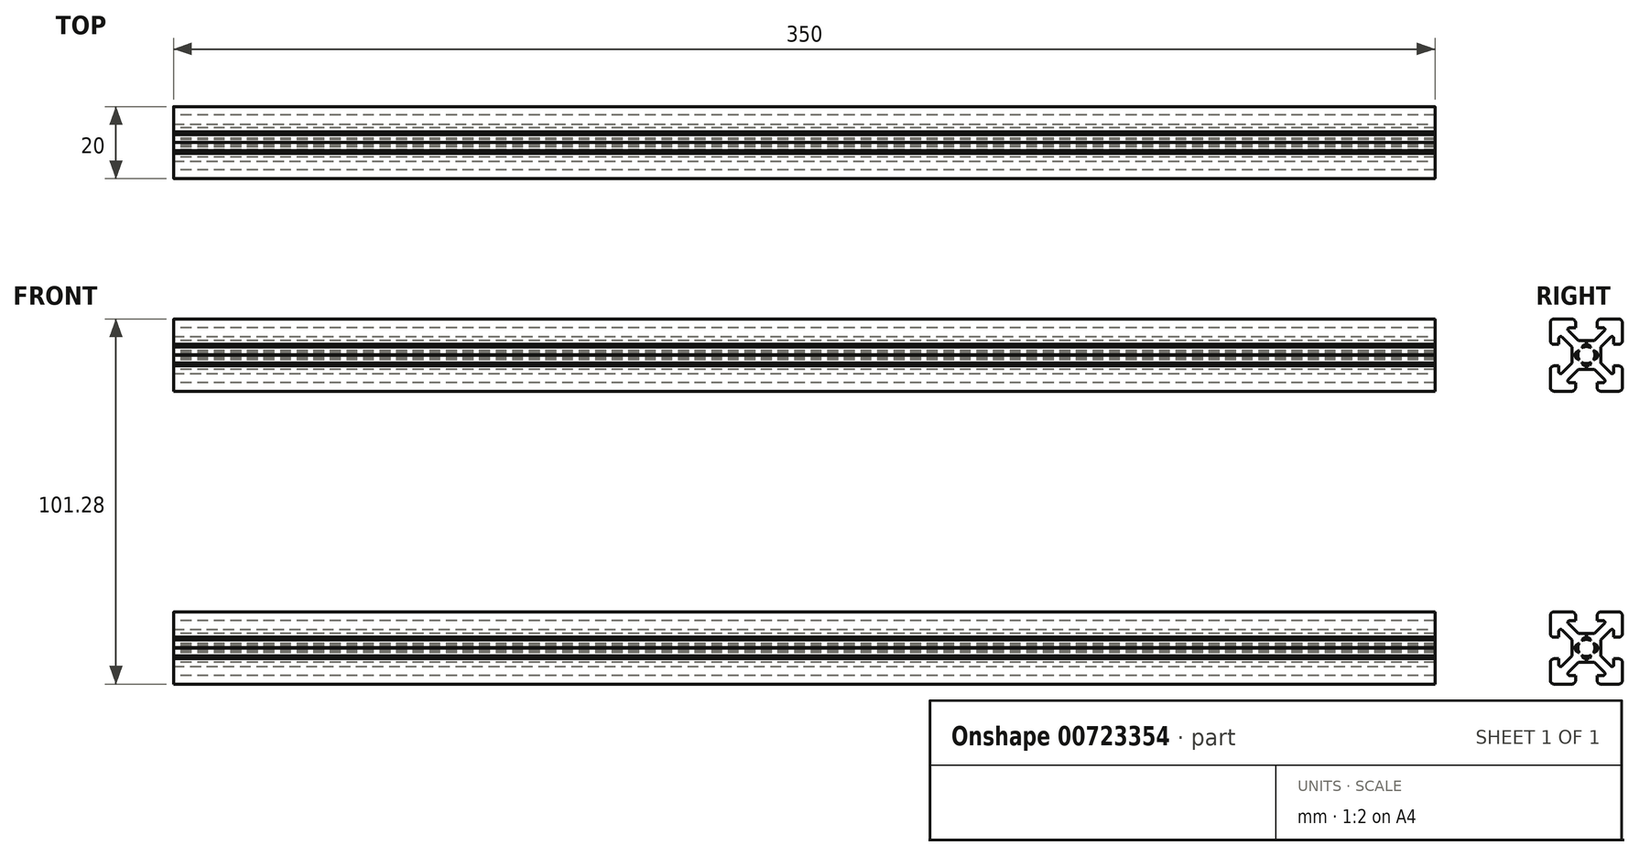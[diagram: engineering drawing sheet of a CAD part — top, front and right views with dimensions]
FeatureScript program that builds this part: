
annotation { "Feature Type Name" : "Feature", "Feature Type Description" : "" }
export const myFeature = defineFeature(function(context is Context, id is Id, definition is map)
    precondition{}
    {
        {
            var Q0;
            Q0=qCreatedBy(makeId("Top.planeOp"),FACE);
            var sketch = newSketch(context, id + "F0", { "sketchPlane" : qUnion([Q0])});
            skLineSegment(sketch, "E0", {"start": v(-15.81, 0) * mm, "end": v(2.4, 0) * mm, "construction": true});
            skLineSegment(sketch, "E1", {"start": v(0, 15.89) * mm, "end": v(0, -13.7) * mm, "construction": true});
            skLineSegment(sketch, "E2", {"start": v(0, 0) * mm, "end": v(-1.66, 1.66) * mm, "construction": true});
            skLineSegment(sketch, "E3", {"start": v(-2.3, 4.06) * mm, "end": v(-5.86, 7.63) * mm});
            skLineSegment(sketch, "E4", {"start": v(-5.86, 7.63) * mm, "end": v(-3, 7.63) * mm});
            skLineSegment(sketch, "E5", {"start": v(-3, 7.63) * mm, "end": v(-3, 10) * mm});
            skLineSegment(sketch, "E6", {"start": v(-3, 10) * mm, "end": v(-10, 10) * mm});
            skLineSegment(sketch, "E7.MirrorCS", {"start": v(-4, 2.23) * mm, "end": v(-7.63, 5.86) * mm});
            skLineSegment(sketch, "E8.MirrorCS", {"start": v(-7.63, 3) * mm, "end": v(-10, 3) * mm});
            skLineSegment(sketch, "E9.MirrorCS", {"start": v(-10, 3) * mm, "end": v(-10, 10) * mm});
            skLineSegment(sketch, "E10.MirrorCS", {"start": v(-7.63, 5.86) * mm, "end": v(-7.63, 3) * mm});
            skLineSegment(sketch, "E11.MirrorCS", {"start": v(3, 10) * mm, "end": v(10, 10) * mm});
            skLineSegment(sketch, "E12.MirrorCS", {"start": v(5.86, 7.63) * mm, "end": v(3, 7.63) * mm});
            skLineSegment(sketch, "E13.MirrorCS", {"start": v(3, 7.63) * mm, "end": v(3, 10) * mm});
            skLineSegment(sketch, "E14.MirrorCS", {"start": v(7.63, 5.86) * mm, "end": v(7.63, 3) * mm});
            skLineSegment(sketch, "E15.MirrorCS", {"start": v(10, 3) * mm, "end": v(10, 10) * mm});
            skLineSegment(sketch, "E16.MirrorCS", {"start": v(7.63, 3) * mm, "end": v(10, 3) * mm});
            skLineSegment(sketch, "E17.MirrorCS", {"start": v(2.3, 4.06) * mm, "end": v(5.86, 7.63) * mm});
            skLineSegment(sketch, "E18.MirrorCS", {"start": v(4, 2.23) * mm, "end": v(7.63, 5.86) * mm});
            skLineSegment(sketch, "E19.MirrorCS", {"start": v(5.86, -7.63) * mm, "end": v(3, -7.63) * mm});
            skLineSegment(sketch, "E20.MirrorCS", {"start": v(3, -10) * mm, "end": v(10, -10) * mm});
            skLineSegment(sketch, "E21.MirrorCS", {"start": v(-5.86, -7.63) * mm, "end": v(-3, -7.63) * mm});
            skLineSegment(sketch, "E22.MirrorCS", {"start": v(-3, -10) * mm, "end": v(-10, -10) * mm});
            skLineSegment(sketch, "E23.MirrorCS", {"start": v(-3, -7.63) * mm, "end": v(-3, -10) * mm});
            skLineSegment(sketch, "E24.MirrorCS", {"start": v(3, -7.63) * mm, "end": v(3, -10) * mm});
            skLineSegment(sketch, "E25.MirrorCS", {"start": v(7.63, -5.86) * mm, "end": v(7.63, -3) * mm});
            skLineSegment(sketch, "E26.MirrorCS", {"start": v(10, -3) * mm, "end": v(10, -10) * mm});
            skLineSegment(sketch, "E27.MirrorCS", {"start": v(4, -2.23) * mm, "end": v(7.63, -5.86) * mm});
            skLineSegment(sketch, "E28.MirrorCS", {"start": v(-7.63, -5.86) * mm, "end": v(-7.63, -3) * mm});
            skLineSegment(sketch, "E29.MirrorCS", {"start": v(-10, -3) * mm, "end": v(-10, -10) * mm});
            skLineSegment(sketch, "E30.MirrorCS", {"start": v(-7.63, -3) * mm, "end": v(-10, -3) * mm});
            skLineSegment(sketch, "E31.MirrorCS", {"start": v(-4, -2.23) * mm, "end": v(-7.63, -5.86) * mm});
            skLineSegment(sketch, "E32.MirrorCS", {"start": v(2.23, -4) * mm, "end": v(5.86, -7.63) * mm});
            skLineSegment(sketch, "E33.MirrorCS", {"start": v(-2.23, -4) * mm, "end": v(-5.86, -7.63) * mm});
            skLineSegment(sketch, "E34.MirrorCS", {"start": v(7.63, -3) * mm, "end": v(10, -3) * mm});
            skLineSegment(sketch, "E35", {"start": v(-4, 0) * mm, "end": v(-4, 0) * mm});
            skLineSegment(sketch, "E36", {"start": v(-2.3, 4.06) * mm, "end": v(-0.02, 4.06) * mm});
            skLineSegment(sketch, "E37.MirrorCS", {"start": v(-15.81, 8.12) * mm, "end": v(21.32, 8.12) * mm, "construction": true});
            skLineSegment(sketch, "E38", {"start": v(-4, 2.23) * mm, "end": v(-4, 0.02) * mm});
            skLineSegment(sketch, "E39", {"start": v(-2.23, -4) * mm, "end": v(-0.05, -4) * mm});
            skLineSegment(sketch, "E40", {"start": v(4, 2.23) * mm, "end": v(4, 0.03) * mm});
            skPoint(sketch, "E41.orphan", {"position": v(-0.59, 2.36) * mm});
            skPoint(sketch, "E42.orphan", {"position": v(-2.36, 0.59) * mm});
            skLineSegment(sketch, "E43.trimOffspring", {"start": v(0.03, 4.06) * mm, "end": v(2.3, 4.06) * mm});
            skPoint(sketch, "E44.orphan", {"position": v(0.59, 2.36) * mm});
            skPoint(sketch, "E45.orphan", {"position": v(2.36, 0.59) * mm});
            skPoint(sketch, "E46.orphan", {"position": v(-2.36, -0.59) * mm});
            skPoint(sketch, "E47.orphan", {"position": v(-0.59, -2.36) * mm});
            skPoint(sketch, "E48.orphan", {"position": v(0.59, -2.36) * mm});
            skPoint(sketch, "E49.orphan", {"position": v(2.36, -0.59) * mm});
            skLineSegment(sketch, "E50", {"start": v(-2.4, 0.03) * mm, "end": v(-2.4, 0.03) * mm});
            skLineSegment(sketch, "E51.MirrorCS", {"start": v(-2.4, -0.03) * mm, "end": v(-2.4, -0.03) * mm});
            skLineSegment(sketch, "E52.MirrorCS", {"start": v(2.4, 0.03) * mm, "end": v(2.4, 0.03) * mm});
            skLineSegment(sketch, "E53.MirrorCS", {"start": v(2.4, -0.03) * mm, "end": v(2.4, -0.03) * mm});
            skLineSegment(sketch, "E54.trimOffspring", {"start": v(4, -0.03) * mm, "end": v(4, -2.23) * mm});
            skLineSegment(sketch, "E55.trimOffspring", {"start": v(-4, -0.03) * mm, "end": v(-4, -2.23) * mm});
            skPoint(sketch, "E56.end.orphan", {"position": v(-2.4, 0) * mm});
            skPoint(sketch, "E57.orphan", {"position": v(-4, 0.03) * mm});
            skPoint(sketch, "E58.MirrorCS.end.orphan", {"position": v(2.4, 0) * mm});
            skPoint(sketch, "E58.MirrorCS.start.orphan", {"position": v(2.4, -0.03) * mm});
            skPoint(sketch, "E59.MirrorCS.start.orphan", {"position": v(2.4, 0.03) * mm});
            skLineSegment(sketch, "E60.trimOffspring", {"start": v(0.05, -4) * mm, "end": v(2.23, -4) * mm});
            skLineSegment(sketch, "E61", {"start": v(0, 0) * mm, "end": v(10, 10) * mm, "construction": true});
            skLineSegment(sketch, "E62", {"start": v(0, 0) * mm, "end": v(-10, -10) * mm, "construction": true});
            skLineSegment(sketch, "E63", {"start": v(10, -10) * mm, "end": v(0.07, 0.07) * mm, "construction": true});
            skPoint(sketch, "E64.start.orphan", {"position": v(-4, -0.03) * mm});
            skLineSegment(sketch, "E65", {"start": v(-2.82, -0.78) * mm, "end": v(-1.9, -1.37) * mm});
            skPoint(sketch, "E66.orphan", {"position": v(-1.66, -1.66) * mm});
            skPoint(sketch, "E67.orphan", {"position": v(0.03, -4.06) * mm});
            skPoint(sketch, "E68.orphan", {"position": v(-0.03, -4.06) * mm});
            skLineSegment(sketch, "E69", {"start": v(-2.82, 0.8) * mm, "end": v(-1.87, 1.41) * mm});
            skLineSegment(sketch, "E70", {"start": v(-0.76, 2.95) * mm, "end": v(-1.54, 1.77) * mm});
            skLineSegment(sketch, "E71", {"start": v(0.76, 2.95) * mm, "end": v(1.51, 1.8) * mm});
            skLineSegment(sketch, "E72", {"start": v(2.82, 0.8) * mm, "end": v(1.83, 1.46) * mm});
            skLineSegment(sketch, "E73", {"start": v(2.82, -0.8) * mm, "end": v(1.87, -1.41) * mm});
            skLineSegment(sketch, "E74.trimOffspring", {"start": v(1.8, -1.68) * mm, "end": v(1.82, -1.66) * mm});
            skLineSegment(sketch, "E75.trimOffspring", {"start": v(-8.12, 8.12) * mm, "end": v(-29.35, 29.35) * mm, "construction": true});
            skLineSegment(sketch, "E76", {"start": v(0.74, -2.96) * mm, "end": v(1.51, -1.8) * mm});
            skPoint(sketch, "E77.trimOffspring.start.orphan", {"position": v(0.33, -2.4) * mm});
            skPoint(sketch, "E78.MirrorCS.end.orphan", {"position": v(-0.33, -2.4) * mm});
            skLineSegment(sketch, "E79.trimOffspring", {"start": v(2.43, 0) * mm, "end": v(21.32, 0) * mm, "construction": true});
            skPoint(sketch, "E80.trimOffspring.start.orphan", {"position": v(0.33, 2.4) * mm});
            skPoint(sketch, "E81.trimOffspring.start.orphan", {"position": v(-0.33, 2.4) * mm});
            skArc(sketch, "E82", {"start": v(-1.87, 1.41) * mm, "mid": v(-2.35, 0.03) * mm, "end": v(-1.9, -1.37) * mm});
            skArc(sketch, "E83.trimOffspring", {"start": v(1.51, 1.8) * mm, "mid": v(-0.02, 2.35) * mm, "end": v(-1.54, 1.77) * mm});
            skArc(sketch, "E84.trimOffspring", {"start": v(1.87, -1.41) * mm, "mid": v(2.35, 0.03) * mm, "end": v(1.83, 1.46) * mm});
            skArc(sketch, "E85.trimOffspring", {"start": v(-1.55, -1.76) * mm, "mid": v(-0.03, -2.35) * mm, "end": v(1.51, -1.8) * mm});
            skLineSegment(sketch, "E86", {"start": v(-1.55, -1.76) * mm, "end": v(-0.75, -2.96) * mm});
            skLineSegment(sketch, "E87", {"start": v(-4, 0.03) * mm, "end": v(-2.82, 0.03) * mm});
            skLineSegment(sketch, "E88", {"start": v(-2.82, 0.03) * mm, "end": v(-2.82, 0.8) * mm});
            skLineSegment(sketch, "E89", {"start": v(-4, -0.03) * mm, "end": v(-2.82, -0.03) * mm});
            skLineSegment(sketch, "E90", {"start": v(-2.82, -0.03) * mm, "end": v(-2.82, -0.78) * mm});
            skLineSegment(sketch, "E91.MirrorCS", {"start": v(4, 0.03) * mm, "end": v(2.82, 0.03) * mm});
            skLineSegment(sketch, "E92.MirrorCS", {"start": v(4, -0.03) * mm, "end": v(2.82, -0.03) * mm});
            skLineSegment(sketch, "E93", {"start": v(2.82, 0.03) * mm, "end": v(2.82, 0.8) * mm});
            skLineSegment(sketch, "E94", {"start": v(2.82, -0.03) * mm, "end": v(2.82, -0.8) * mm});
            skLineSegment(sketch, "E95", {"start": v(-0.05, -4) * mm, "end": v(-0.05, -2.96) * mm});
            skLineSegment(sketch, "E96", {"start": v(-0.05, -2.96) * mm, "end": v(-0.75, -2.96) * mm});
            skLineSegment(sketch, "E97", {"start": v(0.05, -4) * mm, "end": v(0.05, -2.96) * mm});
            skLineSegment(sketch, "E98", {"start": v(0.05, -2.96) * mm, "end": v(0.74, -2.96) * mm});
            skLineSegment(sketch, "E99", {"start": v(-0.02, 4.06) * mm, "end": v(-0.02, 2.95) * mm});
            skLineSegment(sketch, "E100", {"start": v(-0.02, 2.95) * mm, "end": v(-0.76, 2.95) * mm});
            skLineSegment(sketch, "E101", {"start": v(0.03, 4.06) * mm, "end": v(0.03, 2.95) * mm});
            skLineSegment(sketch, "E102", {"start": v(0.03, 2.95) * mm, "end": v(0.76, 2.95) * mm});
            skSolve(sketch);
        }
        {
            var Q0;
            Q0=qSketchRegion(id+"F0",true);
            extrude(context, id + "F1", {"entities" : qUnion([Q0]), "depth" : 350 * mm, "offsetDistance" : 25.4 * mm});
        }
        {
            var Q0;
            Q0=makeQuery(id+"F1.opExtrude","SWEPT_EDGE",EDGE,{"disambiguationData":[OSD([sQuery(id+"F0.wireOp",EDGE,"E15.MirrorCS"),sQuery(id+"F0.wireOp",EDGE,"E11.MirrorCS")])]});
            var Q1;
            Q1=makeQuery(id+"F1.opExtrude","SWEPT_EDGE",EDGE,{"disambiguationData":[OSD([sQuery(id+"F0.wireOp",EDGE,"E20.MirrorCS"),sQuery(id+"F0.wireOp",EDGE,"E26.MirrorCS")])]});
            var Q2;
            Q2=makeQuery(id+"F1.opExtrude","SWEPT_EDGE",EDGE,{"disambiguationData":[OSD([sQuery(id+"F0.wireOp",EDGE,"E22.MirrorCS"),sQuery(id+"F0.wireOp",EDGE,"E29.MirrorCS")])]});
            var Q3;
            Q3=makeQuery(id+"F1.opExtrude","SWEPT_EDGE",EDGE,{"disambiguationData":[OSD([sQuery(id+"F0.wireOp",EDGE,"E22.MirrorCS"),sQuery(id+"F0.wireOp",EDGE,"E23.MirrorCS")])]});
            var Q4;
            Q4=makeQuery(id+"F1.opExtrude","SWEPT_EDGE",EDGE,{"disambiguationData":[OSD([sQuery(id+"F0.wireOp",EDGE,"E20.MirrorCS"),sQuery(id+"F0.wireOp",EDGE,"E24.MirrorCS")])]});
            var Q5;
            Q5=makeQuery(id+"F1.opExtrude","SWEPT_EDGE",EDGE,{"disambiguationData":[OSD([sQuery(id+"F0.wireOp",EDGE,"E5"),sQuery(id+"F0.wireOp",EDGE,"E6")])]});
            var Q6;
            Q6=makeQuery(id+"F1.opExtrude","SWEPT_EDGE",EDGE,{"disambiguationData":[OSD([sQuery(id+"F0.wireOp",EDGE,"E8.MirrorCS"),sQuery(id+"F0.wireOp",EDGE,"E9.MirrorCS")])]});
            var Q7;
            Q7=makeQuery(id+"F1.opExtrude","SWEPT_EDGE",EDGE,{"disambiguationData":[OSD([sQuery(id+"F0.wireOp",EDGE,"E15.MirrorCS"),sQuery(id+"F0.wireOp",EDGE,"E16.MirrorCS")])]});
            var Q8;
            Q8=makeQuery(id+"F1.opExtrude","SWEPT_EDGE",EDGE,{"disambiguationData":[OSD([sQuery(id+"F0.wireOp",EDGE,"E26.MirrorCS"),sQuery(id+"F0.wireOp",EDGE,"E34.MirrorCS")])]});
            var Q9;
            Q9=makeQuery(id+"F1.opExtrude","SWEPT_EDGE",EDGE,{"disambiguationData":[OSD([sQuery(id+"F0.wireOp",EDGE,"E29.MirrorCS"),sQuery(id+"F0.wireOp",EDGE,"E30.MirrorCS")])]});
            var Q10;
            Q10=makeQuery(id+"F1.opExtrude","SWEPT_EDGE",EDGE,{"disambiguationData":[OSD([sQuery(id+"F0.wireOp",EDGE,"E9.MirrorCS"),sQuery(id+"F0.wireOp",EDGE,"E6")])]});
            var Q11;
            Q11=makeQuery(id+"F1.opExtrude","SWEPT_EDGE",EDGE,{"disambiguationData":[OSD([sQuery(id+"F0.wireOp",EDGE,"E13.MirrorCS"),sQuery(id+"F0.wireOp",EDGE,"E11.MirrorCS")])]});
            fillet(context, id + "F2", {"entities" : qUnion([Q0, Q1, Q2, Q3, Q4, Q5, Q6, Q7, Q8, Q9, Q10, Q11]), "radius" : 1 * mm, "tangentPropagation" : true, "allowEdgeOverflow" : false});
        }
        {
            var Q0;
            Q0=makeQuery(id+"F1.opExtrude","SWEPT_EDGE",EDGE,{"disambiguationData":[OSD([sQuery(id+"F0.wireOp",EDGE,"E7.MirrorCS"),sQuery(id+"F0.wireOp",EDGE,"E10.MirrorCS")])]});
            var Q1;
            Q1=makeQuery(id+"F1.opExtrude","SWEPT_EDGE",EDGE,{"disambiguationData":[OSD([sQuery(id+"F0.wireOp",EDGE,"E3"),sQuery(id+"F0.wireOp",EDGE,"E4")])]});
            var Q2;
            Q2=makeQuery(id+"F1.opExtrude","SWEPT_EDGE",EDGE,{"disambiguationData":[OSD([sQuery(id+"F0.wireOp",EDGE,"E12.MirrorCS"),sQuery(id+"F0.wireOp",EDGE,"E17.MirrorCS")])]});
            var Q3;
            Q3=makeQuery(id+"F1.opExtrude","SWEPT_EDGE",EDGE,{"disambiguationData":[OSD([sQuery(id+"F0.wireOp",EDGE,"E14.MirrorCS"),sQuery(id+"F0.wireOp",EDGE,"E18.MirrorCS")])]});
            var Q4;
            Q4=makeQuery(id+"F1.opExtrude","SWEPT_EDGE",EDGE,{"disambiguationData":[OSD([sQuery(id+"F0.wireOp",EDGE,"E28.MirrorCS"),sQuery(id+"F0.wireOp",EDGE,"E31.MirrorCS")])]});
            var Q5;
            Q5=makeQuery(id+"F1.opExtrude","SWEPT_EDGE",EDGE,{"disambiguationData":[OSD([sQuery(id+"F0.wireOp",EDGE,"E21.MirrorCS"),sQuery(id+"F0.wireOp",EDGE,"E33.MirrorCS")])]});
            var Q6;
            Q6=makeQuery(id+"F1.opExtrude","SWEPT_EDGE",EDGE,{"disambiguationData":[OSD([sQuery(id+"F0.wireOp",EDGE,"E19.MirrorCS"),sQuery(id+"F0.wireOp",EDGE,"E32.MirrorCS")])]});
            var Q7;
            Q7=makeQuery(id+"F1.opExtrude","SWEPT_EDGE",EDGE,{"disambiguationData":[OSD([sQuery(id+"F0.wireOp",EDGE,"E25.MirrorCS"),sQuery(id+"F0.wireOp",EDGE,"E27.MirrorCS")])]});
            fillet(context, id + "F3", {"entities" : qUnion([Q0, Q1, Q2, Q3, Q4, Q5, Q6, Q7]), "radius" : .5 * mm, "tangentPropagation" : true, "allowEdgeOverflow" : false});
        }
        {
            var Q0;
            Q0=makeQuery(id+"F1.opExtrude","SWEPT_EDGE",EDGE,{"disambiguationData":[OSD([sQuery(id+"F0.wireOp",EDGE,"E69"),sQuery(id+"F0.wireOp",EDGE,"E82")])]});
            var Q1;
            Q1=makeQuery(id+"F1.opExtrude","SWEPT_EDGE",EDGE,{"disambiguationData":[OSD([sQuery(id+"F0.wireOp",EDGE,"E17.MirrorCS"),sQuery(id+"F0.wireOp",EDGE,"E43.trimOffspring")])]});
            var Q2;
            {var subQ0=sQuery(id+"F0.wireOp",EDGE,"E12.MirrorCS");Q2=makeQuery(id+"F3.opFillet","BLEND_EDGE",EDGE,{"blendedFrom":[makeQuery(id+"F1.opExtrude","SWEPT_EDGE",EDGE,{"disambiguationData":[OSD([subQ0,sQuery(id+"F0.wireOp",EDGE,"E17.MirrorCS")])]}),makeQuery(id+"F1.opExtrude","SWEPT_FACE",FACE,{"disambiguationData":[OSD([subQ0])]})],"blendedInto":[makeQuery(id+"F1.opExtrude","SWEPT_FACE",FACE,{"disambiguationData":[OSD([subQ0])]})]});}
            var Q3;
            Q3=makeQuery(id+"F1.opExtrude","SWEPT_EDGE",EDGE,{"disambiguationData":[OSD([sQuery(id+"F0.wireOp",EDGE,"E70"),sQuery(id+"F0.wireOp",EDGE,"E83.trimOffspring")])]});
            var Q4;
            Q4=makeQuery(id+"F1.opExtrude","SWEPT_EDGE",EDGE,{"disambiguationData":[OSD([sQuery(id+"F0.wireOp",EDGE,"VnvyymTW-JKNP-Vp1J-SOXt-zXPDHYCny5Fm"),sQuery(id+"F0.wireOp",EDGE,"E85.trimOffspring")])]});
            var Q5;
            Q5=makeQuery(id+"F1.opExtrude","SWEPT_EDGE",EDGE,{"disambiguationData":[OSD([sQuery(id+"F0.wireOp",EDGE,"E76"),sQuery(id+"F0.wireOp",EDGE,"E85.trimOffspring")])]});
            var Q6;
            Q6=makeQuery(id+"F1.opExtrude","SWEPT_EDGE",EDGE,{"disambiguationData":[OSD([sQuery(id+"F0.wireOp",EDGE,"E73"),sQuery(id+"F0.wireOp",EDGE,"E84.trimOffspring")])]});
            var Q7;
            Q7=makeQuery(id+"F1.opExtrude","SWEPT_EDGE",EDGE,{"disambiguationData":[OSD([sQuery(id+"F0.wireOp",EDGE,"E72"),sQuery(id+"F0.wireOp",EDGE,"E84.trimOffspring")])]});
            var Q8;
            Q8=makeQuery(id+"F1.opExtrude","SWEPT_EDGE",EDGE,{"disambiguationData":[OSD([sQuery(id+"F0.wireOp",EDGE,"E71"),sQuery(id+"F0.wireOp",EDGE,"E83.trimOffspring")])]});
            var Q9;
            Q9=makeQuery(id+"F1.opExtrude","SWEPT_EDGE",EDGE,{"disambiguationData":[OSD([sQuery(id+"F0.wireOp",EDGE,"E65"),sQuery(id+"F0.wireOp",EDGE,"E82")])]});
            fillet(context, id + "F4", {"entities" : qUnion([Q0, Q1, Q2, Q3, Q4, Q5, Q6, Q7, Q8, Q9]), "radius" : .1 * mm, "tangentPropagation" : true, "allowEdgeOverflow" : false});
        }
        {
            var Q0;
            Q0=makeQuery(id+"F1.opExtrude","SWEPT_BODY",BODY,{"disambiguationData":[OSD([sQuery(id+"F0.wireOp",EDGE,"E3"),sQuery(id+"F0.wireOp",EDGE,"E7.MirrorCS"),sQuery(id+"F0.wireOp",EDGE,"E8.MirrorCS"),sQuery(id+"F0.wireOp",EDGE,"E9.MirrorCS"),sQuery(id+"F0.wireOp",EDGE,"E10.MirrorCS"),sQuery(id+"F0.wireOp",EDGE,"E5"),sQuery(id+"F0.wireOp",EDGE,"E6"),sQuery(id+"F0.wireOp",EDGE,"E4"),sQuery(id+"F0.wireOp",EDGE,"E14.MirrorCS"),sQuery(id+"F0.wireOp",EDGE,"E15.MirrorCS"),sQuery(id+"F0.wireOp",EDGE,"E16.MirrorCS"),sQuery(id+"F0.wireOp",EDGE,"E12.MirrorCS"),sQuery(id+"F0.wireOp",EDGE,"E17.MirrorCS"),sQuery(id+"F0.wireOp",EDGE,"E18.MirrorCS"),sQuery(id+"F0.wireOp",EDGE,"E13.MirrorCS"),sQuery(id+"F0.wireOp",EDGE,"E11.MirrorCS"),sQuery(id+"F0.wireOp",EDGE,"E21.MirrorCS"),sQuery(id+"F0.wireOp",EDGE,"E19.MirrorCS"),sQuery(id+"F0.wireOp",EDGE,"E20.MirrorCS"),sQuery(id+"F0.wireOp",EDGE,"E24.MirrorCS"),sQuery(id+"F0.wireOp",EDGE,"E25.MirrorCS"),sQuery(id+"F0.wireOp",EDGE,"E26.MirrorCS"),sQuery(id+"F0.wireOp",EDGE,"E27.MirrorCS"),sQuery(id+"F0.wireOp",EDGE,"E22.MirrorCS"),sQuery(id+"F0.wireOp",EDGE,"E28.MirrorCS"),sQuery(id+"F0.wireOp",EDGE,"E29.MirrorCS"),sQuery(id+"F0.wireOp",EDGE,"E30.MirrorCS"),sQuery(id+"F0.wireOp",EDGE,"E31.MirrorCS"),sQuery(id+"F0.wireOp",EDGE,"E23.MirrorCS"),sQuery(id+"F0.wireOp",EDGE,"E32.MirrorCS"),sQuery(id+"F0.wireOp",EDGE,"E33.MirrorCS"),sQuery(id+"F0.wireOp",EDGE,"E34.MirrorCS"),sQuery(id+"F0.wireOp",EDGE,"E36"),sQuery(id+"F0.wireOp",EDGE,"E38"),sQuery(id+"F0.wireOp",EDGE,"E39"),sQuery(id+"F0.wireOp",EDGE,"E40"),sQuery(id+"F0.wireOp",EDGE,"E43.trimOffspring"),sQuery(id+"F0.wireOp",EDGE,"E54.trimOffspring"),sQuery(id+"F0.wireOp",EDGE,"E55.trimOffspring"),sQuery(id+"F0.wireOp",EDGE,"E60.trimOffspring"),sQuery(id+"F0.wireOp",EDGE,"E65"),sQuery(id+"F0.wireOp",EDGE,"E69"),sQuery(id+"F0.wireOp",EDGE,"E70"),sQuery(id+"F0.wireOp",EDGE,"E71"),sQuery(id+"F0.wireOp",EDGE,"E72"),sQuery(id+"F0.wireOp",EDGE,"E73"),sQuery(id+"F0.wireOp",EDGE,"E76"),sQuery(id+"F0.wireOp",EDGE,"E82"),sQuery(id+"F0.wireOp",EDGE,"E83.trimOffspring"),sQuery(id+"F0.wireOp",EDGE,"E84.trimOffspring"),sQuery(id+"F0.wireOp",EDGE,"E85.trimOffspring"),sQuery(id+"F0.wireOp",EDGE,"E86"),sQuery(id+"F0.wireOp",EDGE,"E87"),sQuery(id+"F0.wireOp",EDGE,"E88"),sQuery(id+"F0.wireOp",EDGE,"E89"),sQuery(id+"F0.wireOp",EDGE,"E90"),sQuery(id+"F0.wireOp",EDGE,"E91.MirrorCS"),sQuery(id+"F0.wireOp",EDGE,"E92.MirrorCS"),sQuery(id+"F0.wireOp",EDGE,"E93"),sQuery(id+"F0.wireOp",EDGE,"E94"),sQuery(id+"F0.wireOp",EDGE,"E95"),sQuery(id+"F0.wireOp",EDGE,"E96"),sQuery(id+"F0.wireOp",EDGE,"E97"),sQuery(id+"F0.wireOp",EDGE,"E98"),sQuery(id+"F0.wireOp",EDGE,"E99"),sQuery(id+"F0.wireOp",EDGE,"E100"),sQuery(id+"F0.wireOp",EDGE,"E101"),sQuery(id+"F0.wireOp",EDGE,"E102")])]});
            var Q1;
            Q1=makeQuery(id+"F1.opExtrude","CAP_EDGE",EDGE,{"disambiguationData":[OSD([sQuery(id+"F0.wireOp",EDGE,"E15.MirrorCS")])],"isStart":false});
            transform(context, id + "F5", {"entities" : qUnion([Q0]), "transformType" : TransformType.ROTATION, "transformAxis" : qUnion([Q1]), "angle" : 90 * degree, "makeCopy" : false});
        }
        {
            var Q0;
            Q0=makeQuery(id+"F1.opExtrude","SWEPT_BODY",BODY,{"disambiguationData":[OSD([sQuery(id+"F0.wireOp",EDGE,"E3"),sQuery(id+"F0.wireOp",EDGE,"E7.MirrorCS"),sQuery(id+"F0.wireOp",EDGE,"E8.MirrorCS"),sQuery(id+"F0.wireOp",EDGE,"E9.MirrorCS"),sQuery(id+"F0.wireOp",EDGE,"E10.MirrorCS"),sQuery(id+"F0.wireOp",EDGE,"E5"),sQuery(id+"F0.wireOp",EDGE,"E6"),sQuery(id+"F0.wireOp",EDGE,"E4"),sQuery(id+"F0.wireOp",EDGE,"E14.MirrorCS"),sQuery(id+"F0.wireOp",EDGE,"E15.MirrorCS"),sQuery(id+"F0.wireOp",EDGE,"E16.MirrorCS"),sQuery(id+"F0.wireOp",EDGE,"E12.MirrorCS"),sQuery(id+"F0.wireOp",EDGE,"E17.MirrorCS"),sQuery(id+"F0.wireOp",EDGE,"E18.MirrorCS"),sQuery(id+"F0.wireOp",EDGE,"E13.MirrorCS"),sQuery(id+"F0.wireOp",EDGE,"E11.MirrorCS"),sQuery(id+"F0.wireOp",EDGE,"E21.MirrorCS"),sQuery(id+"F0.wireOp",EDGE,"E19.MirrorCS"),sQuery(id+"F0.wireOp",EDGE,"E20.MirrorCS"),sQuery(id+"F0.wireOp",EDGE,"E24.MirrorCS"),sQuery(id+"F0.wireOp",EDGE,"E25.MirrorCS"),sQuery(id+"F0.wireOp",EDGE,"E26.MirrorCS"),sQuery(id+"F0.wireOp",EDGE,"E27.MirrorCS"),sQuery(id+"F0.wireOp",EDGE,"E22.MirrorCS"),sQuery(id+"F0.wireOp",EDGE,"E28.MirrorCS"),sQuery(id+"F0.wireOp",EDGE,"E29.MirrorCS"),sQuery(id+"F0.wireOp",EDGE,"E30.MirrorCS"),sQuery(id+"F0.wireOp",EDGE,"E31.MirrorCS"),sQuery(id+"F0.wireOp",EDGE,"E23.MirrorCS"),sQuery(id+"F0.wireOp",EDGE,"E32.MirrorCS"),sQuery(id+"F0.wireOp",EDGE,"E33.MirrorCS"),sQuery(id+"F0.wireOp",EDGE,"E34.MirrorCS"),sQuery(id+"F0.wireOp",EDGE,"E36"),sQuery(id+"F0.wireOp",EDGE,"E38"),sQuery(id+"F0.wireOp",EDGE,"E39"),sQuery(id+"F0.wireOp",EDGE,"E40"),sQuery(id+"F0.wireOp",EDGE,"E43.trimOffspring"),sQuery(id+"F0.wireOp",EDGE,"E54.trimOffspring"),sQuery(id+"F0.wireOp",EDGE,"E55.trimOffspring"),sQuery(id+"F0.wireOp",EDGE,"E60.trimOffspring"),sQuery(id+"F0.wireOp",EDGE,"E65"),sQuery(id+"F0.wireOp",EDGE,"E69"),sQuery(id+"F0.wireOp",EDGE,"E70"),sQuery(id+"F0.wireOp",EDGE,"E71"),sQuery(id+"F0.wireOp",EDGE,"E72"),sQuery(id+"F0.wireOp",EDGE,"E73"),sQuery(id+"F0.wireOp",EDGE,"E76"),sQuery(id+"F0.wireOp",EDGE,"E82"),sQuery(id+"F0.wireOp",EDGE,"E83.trimOffspring"),sQuery(id+"F0.wireOp",EDGE,"E84.trimOffspring"),sQuery(id+"F0.wireOp",EDGE,"E85.trimOffspring"),sQuery(id+"F0.wireOp",EDGE,"E86"),sQuery(id+"F0.wireOp",EDGE,"E87"),sQuery(id+"F0.wireOp",EDGE,"E88"),sQuery(id+"F0.wireOp",EDGE,"E89"),sQuery(id+"F0.wireOp",EDGE,"E90"),sQuery(id+"F0.wireOp",EDGE,"E91.MirrorCS"),sQuery(id+"F0.wireOp",EDGE,"E92.MirrorCS"),sQuery(id+"F0.wireOp",EDGE,"E93"),sQuery(id+"F0.wireOp",EDGE,"E94"),sQuery(id+"F0.wireOp",EDGE,"E95"),sQuery(id+"F0.wireOp",EDGE,"E96"),sQuery(id+"F0.wireOp",EDGE,"E97"),sQuery(id+"F0.wireOp",EDGE,"E98"),sQuery(id+"F0.wireOp",EDGE,"E99"),sQuery(id+"F0.wireOp",EDGE,"E100"),sQuery(id+"F0.wireOp",EDGE,"E101"),sQuery(id+"F0.wireOp",EDGE,"E102")])]});
            transform(context, id + "F6", {"entities" : qUnion([Q0]), "transformType" : TransformType.TRANSLATION_3D, "dx" : 0 * mm, "dy" : 0 * mm, "dz" : -350.52 * mm, "makeCopy" : false});
        }
        {
            var Q0;
            Q0=makeQuery(id+"F1.opExtrude","SWEPT_BODY",BODY,{"disambiguationData":[OSD([sQuery(id+"F0.wireOp",EDGE,"E3"),sQuery(id+"F0.wireOp",EDGE,"E7.MirrorCS"),sQuery(id+"F0.wireOp",EDGE,"E8.MirrorCS"),sQuery(id+"F0.wireOp",EDGE,"E9.MirrorCS"),sQuery(id+"F0.wireOp",EDGE,"E10.MirrorCS"),sQuery(id+"F0.wireOp",EDGE,"E5"),sQuery(id+"F0.wireOp",EDGE,"E6"),sQuery(id+"F0.wireOp",EDGE,"E4"),sQuery(id+"F0.wireOp",EDGE,"E14.MirrorCS"),sQuery(id+"F0.wireOp",EDGE,"E15.MirrorCS"),sQuery(id+"F0.wireOp",EDGE,"E16.MirrorCS"),sQuery(id+"F0.wireOp",EDGE,"E12.MirrorCS"),sQuery(id+"F0.wireOp",EDGE,"E17.MirrorCS"),sQuery(id+"F0.wireOp",EDGE,"E18.MirrorCS"),sQuery(id+"F0.wireOp",EDGE,"E13.MirrorCS"),sQuery(id+"F0.wireOp",EDGE,"E11.MirrorCS"),sQuery(id+"F0.wireOp",EDGE,"E21.MirrorCS"),sQuery(id+"F0.wireOp",EDGE,"E19.MirrorCS"),sQuery(id+"F0.wireOp",EDGE,"E20.MirrorCS"),sQuery(id+"F0.wireOp",EDGE,"E24.MirrorCS"),sQuery(id+"F0.wireOp",EDGE,"E25.MirrorCS"),sQuery(id+"F0.wireOp",EDGE,"E26.MirrorCS"),sQuery(id+"F0.wireOp",EDGE,"E27.MirrorCS"),sQuery(id+"F0.wireOp",EDGE,"E22.MirrorCS"),sQuery(id+"F0.wireOp",EDGE,"E28.MirrorCS"),sQuery(id+"F0.wireOp",EDGE,"E29.MirrorCS"),sQuery(id+"F0.wireOp",EDGE,"E30.MirrorCS"),sQuery(id+"F0.wireOp",EDGE,"E31.MirrorCS"),sQuery(id+"F0.wireOp",EDGE,"E23.MirrorCS"),sQuery(id+"F0.wireOp",EDGE,"E32.MirrorCS"),sQuery(id+"F0.wireOp",EDGE,"E33.MirrorCS"),sQuery(id+"F0.wireOp",EDGE,"E34.MirrorCS"),sQuery(id+"F0.wireOp",EDGE,"E36"),sQuery(id+"F0.wireOp",EDGE,"E38"),sQuery(id+"F0.wireOp",EDGE,"E39"),sQuery(id+"F0.wireOp",EDGE,"E40"),sQuery(id+"F0.wireOp",EDGE,"E43.trimOffspring"),sQuery(id+"F0.wireOp",EDGE,"E54.trimOffspring"),sQuery(id+"F0.wireOp",EDGE,"E55.trimOffspring"),sQuery(id+"F0.wireOp",EDGE,"E60.trimOffspring"),sQuery(id+"F0.wireOp",EDGE,"E65"),sQuery(id+"F0.wireOp",EDGE,"E69"),sQuery(id+"F0.wireOp",EDGE,"E70"),sQuery(id+"F0.wireOp",EDGE,"E71"),sQuery(id+"F0.wireOp",EDGE,"E72"),sQuery(id+"F0.wireOp",EDGE,"E73"),sQuery(id+"F0.wireOp",EDGE,"E76"),sQuery(id+"F0.wireOp",EDGE,"E82"),sQuery(id+"F0.wireOp",EDGE,"E83.trimOffspring"),sQuery(id+"F0.wireOp",EDGE,"E84.trimOffspring"),sQuery(id+"F0.wireOp",EDGE,"E85.trimOffspring"),sQuery(id+"F0.wireOp",EDGE,"E86"),sQuery(id+"F0.wireOp",EDGE,"E87"),sQuery(id+"F0.wireOp",EDGE,"E88"),sQuery(id+"F0.wireOp",EDGE,"E89"),sQuery(id+"F0.wireOp",EDGE,"E90"),sQuery(id+"F0.wireOp",EDGE,"E91.MirrorCS"),sQuery(id+"F0.wireOp",EDGE,"E92.MirrorCS"),sQuery(id+"F0.wireOp",EDGE,"E93"),sQuery(id+"F0.wireOp",EDGE,"E94"),sQuery(id+"F0.wireOp",EDGE,"E95"),sQuery(id+"F0.wireOp",EDGE,"E96"),sQuery(id+"F0.wireOp",EDGE,"E97"),sQuery(id+"F0.wireOp",EDGE,"E98"),sQuery(id+"F0.wireOp",EDGE,"E99"),sQuery(id+"F0.wireOp",EDGE,"E100"),sQuery(id+"F0.wireOp",EDGE,"E101"),sQuery(id+"F0.wireOp",EDGE,"E102")])]});
            transform(context, id + "F7", {"entities" : qUnion([Q0]), "transformType" : TransformType.TRANSLATION_3D, "dx" : 0 * mm, "dy" : 0 * mm, "dz" : 81.28 * mm, "makeCopy" : true});
        }
    });
